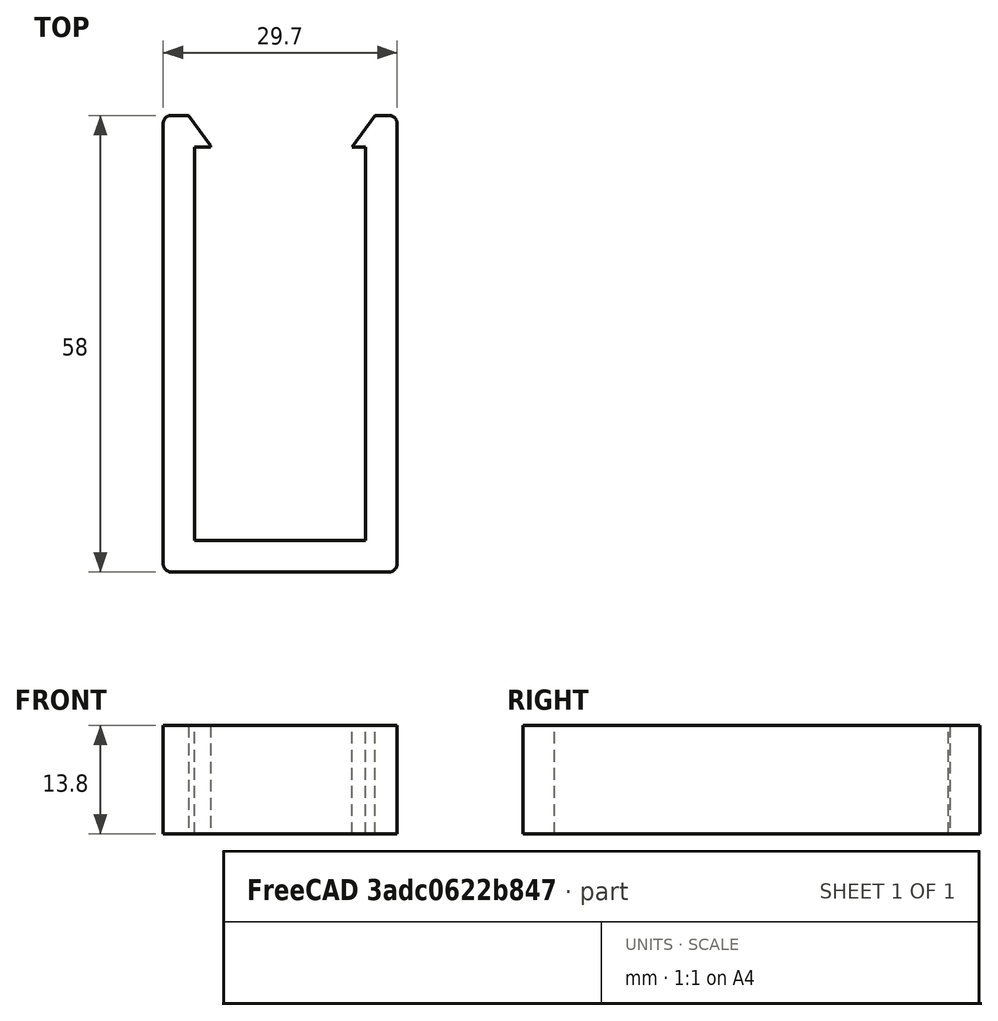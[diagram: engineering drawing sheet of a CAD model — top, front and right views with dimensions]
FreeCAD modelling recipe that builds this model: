
FCSTD DOCUMENT
Label: mediacabinetlock
objects: Part::Box×5, Part::Cut×4, PartDesign::Fillet×2, App::MeasureDistance×1
note: 11 computed .brp shape members not serialized (recipe doc carries the construction recipe); baked Part::Feature solids carry a one-line shape summary decoded from their .brp

FEATURE [Part::Box] Box
  Height = 58
  Length = 29.7
  Width = 13.8
FEATURE [Part::Box] Box001
  Height = 50
  Length = 21.7
  Placement = pos=(4,0,4) rot=(0,0,1;0rad)
  Width = 13.8
FEATURE [Part::Cut] Cut
  Base = -> Box
  Tool = -> Box001
FEATURE [Part::Box] Box002
  Height = 4
  Length = 17.8
  Placement = pos=(6,0,0) rot=(0,0,1;0rad)
  Width = 13.8
FEATURE [Part::Cut] Cut001
  Base = -> Cut
  Tool = -> Box002
FEATURE [App::MeasureDistance] Distance  label="Distance: 21.719"
  Distance = 21.7189
  P1 = (4,0,28.9809)
  P2 = (25.7,0,29.8859)
FEATURE [PartDesign::Fillet] Fillet
  Base = -> Cut001 [Face1,Edge2,Face3,Face14,Edge17]
  Radius = 1
FEATURE [PartDesign::Fillet] Fillet001
  Base = -> Fillet [Face8,Edge34,Face6,Face1,Edge3,Face4]
  Radius = 1
FEATURE [Part::Box] Box003
  Height = 4
  Length = 6
  Placement = pos=(6,0,-3) rot=(0,-1,0;0.942476rad)
  Width = 13.8
FEATURE [Part::Box] Box004
  Height = 4
  Length = 6
  Placement = pos=(20.5,0,2) rot=(0,1,0;0.942476rad)
  Width = 13.8
FEATURE [Part::Cut] Cut002
  Base = -> Fillet001
  Tool = -> Box003
FEATURE [Part::Cut] Cut003
  Base = -> Cut002
  Placement = pos=(0.0255039,0.00024024,5.45958) rot=(1,0,0;1.5708rad)
  Tool = -> Box004
